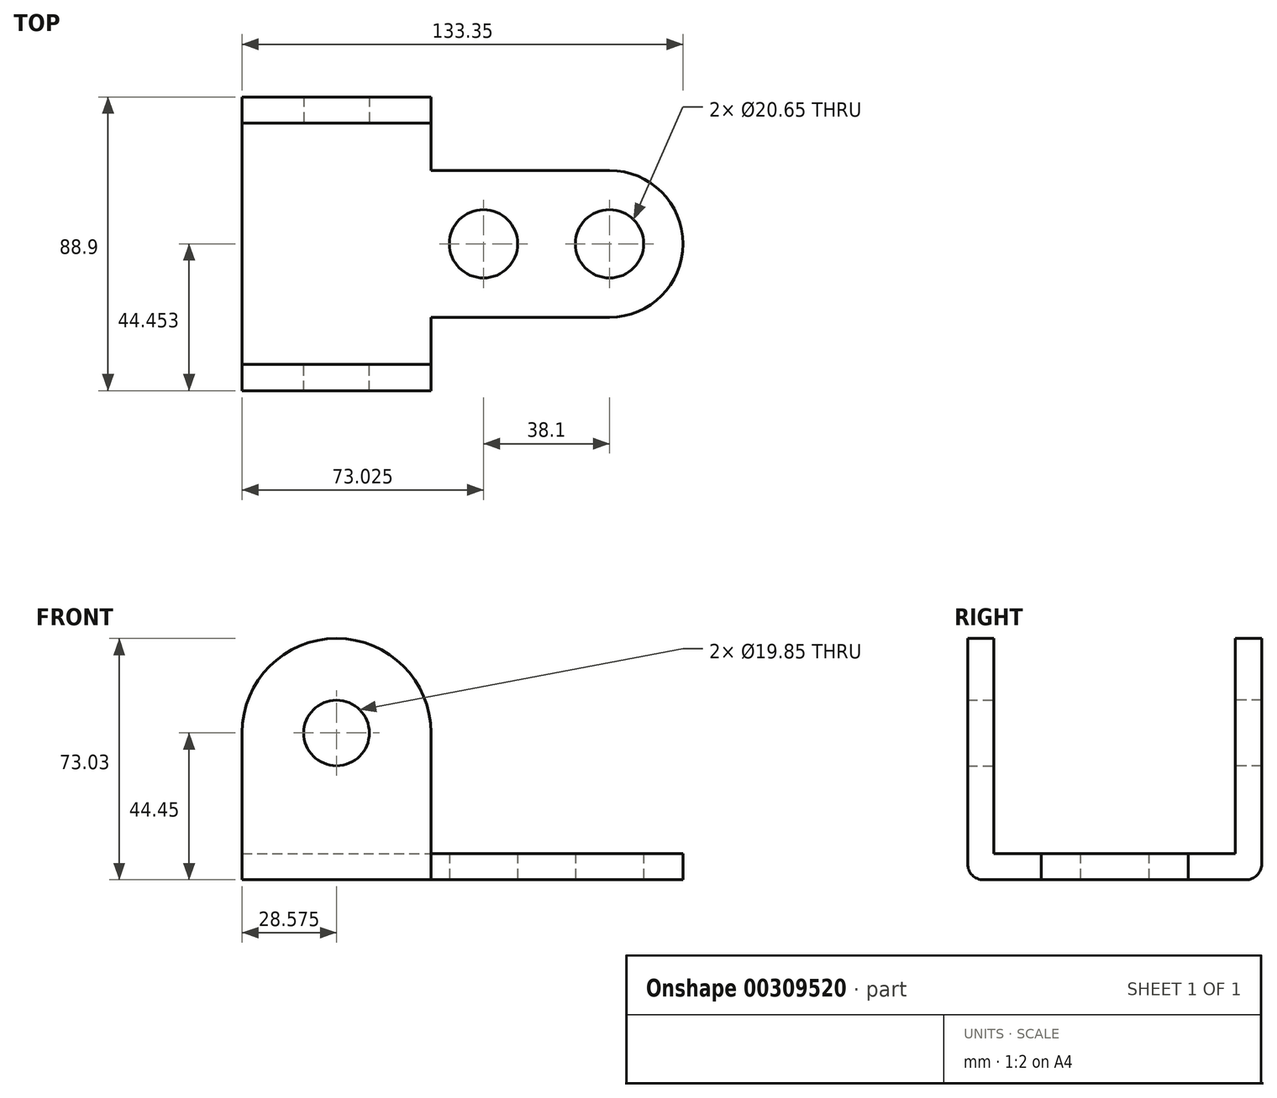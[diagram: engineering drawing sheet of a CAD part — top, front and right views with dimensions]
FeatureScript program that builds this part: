
annotation { "Feature Type Name" : "Feature", "Feature Type Description" : "" }
export const myFeature = defineFeature(function(context is Context, id is Id, definition is map)
    precondition{}
    {
        {
            var Q0;
            Q0=qCreatedBy(makeId("Front.planeOp"),FACE);
            var sketch = newSketch(context, id + "F0", { "sketchPlane" : qUnion([Q0])});
            skLineSegment(sketch, "E0.bottom", {"start": v(0, 0) * mm, "end": v(57.15, 0) * mm});
            skLineSegment(sketch, "E0.left", {"start": v(0, 0) * mm, "end": v(0, 44.45) * mm});
            skLineSegment(sketch, "E0.right", {"start": v(57.15, 0) * mm, "end": v(57.15, 44.45) * mm});
            skCircle(sketch, "E1", {"center": v(28.57, 44.45) * mm, "radius": 9.92 * mm});
            skArc(sketch, "E2", {"start": v(57.15, 44.45) * mm, "mid": v(28.57, 73.03) * mm, "end": v(0, 44.45) * mm});
            skSolve(sketch);
        }
        {
            var Q0;
            Q0 = qSketchRegion(id + "F0", true);
            extrude(context, id + "F1", {"entities" : qUnion([Q0]), "depth" : 7.94 * mm});
        }
        {
            var Q0;
            Q0=qCreatedBy(makeId("Top.planeOp"),FACE);
            var sketch = newSketch(context, id + "F2", { "sketchPlane" : qUnion([Q0])});
            skLineSegment(sketch, "E3.bottom", {"start": v(0, 0) * mm, "end": v(57.15, 0) * mm});
            skLineSegment(sketch, "E3.top", {"start": v(0, 36.51) * mm, "end": v(57.15, 36.51) * mm});
            skLineSegment(sketch, "E3.left", {"start": v(0, 0) * mm, "end": v(0, 36.51) * mm});
            skLineSegment(sketch, "E3.right", {"start": v(57.15, 0) * mm, "end": v(57.15, 36.51) * mm});
            skSolve(sketch);
        }
        {
            var Q0;
            Q0 = qSketchRegion(id + "F2", true);
            extrude(context, id + "F3", {"entities" : qUnion([Q0]), "operationType" : NewBodyOperationType.ADD, "depth" : 7.94 * mm});
        }
        {
            var Q0;
            Q0=makeQuery(id+"F1.opExtrude","SWEPT_BODY",BODY,{"disambiguationData":[OSD([sQuery(id+"F0.wireOp",EDGE,"E0.bottom"),sQuery(id+"F0.wireOp",EDGE,"E0.left"),sQuery(id+"F0.wireOp",EDGE,"E0.right"),sQuery(id+"F0.wireOp",EDGE,"E1"),sQuery(id+"F0.wireOp",EDGE,"E2")])]});
            var Q1;
            Q1=makeQuery(id+"F3.opExtrude","SWEPT_FACE",FACE,{"disambiguationData":[OSD([sQuery(id+"F2.wireOp",EDGE,"E3.top")])]});
            mirror(context, id + "F4", {"operationType" : NewBodyOperationType.ADD, "entities" : qUnion([Q0]), "mirrorPlane" : qUnion([Q1])});
        }
        {
            var Q0;
            Q0=qCreatedBy(makeId("Top.planeOp"),FACE);
            var sketch = newSketch(context, id + "F5", { "sketchPlane" : qUnion([Q0])});
            skLineSegment(sketch, "E4.bottom", {"start": v(57.15, 14.29) * mm, "end": v(111.12, 14.29) * mm});
            skLineSegment(sketch, "E4.top", {"start": v(57.15, 58.74) * mm, "end": v(111.12, 58.74) * mm});
            skLineSegment(sketch, "E4.left", {"start": v(57.15, 14.29) * mm, "end": v(57.15, 58.74) * mm});
            skPoint(sketch, "E5", {"position": v(57.15, 36.51) * mm});
            skArc(sketch, "E6", {"start": v(111.12, 14.29) * mm, "mid": v(133.35, 36.51) * mm, "end": v(111.12, 58.74) * mm});
            skCircle(sketch, "E7", {"center": v(111.12, 36.51) * mm, "radius": 10.33 * mm});
            skCircle(sketch, "E8", {"center": v(73.03, 36.51) * mm, "radius": 10.33 * mm});
            skSolve(sketch);
        }
        {
            var Q0;
            Q0 = qSketchRegion(id + "F5", true);
            extrude(context, id + "F6", {"entities" : qUnion([Q0]), "operationType" : NewBodyOperationType.ADD, "depth" : 7.94 * mm});
        }
        {
            var Q0;
            Q0=makeQuery(id+"F4.opPattern","COPY",EDGE,{"derivedFrom":makeQuery(id+"F3.opExtrude","CAP_EDGE",EDGE,{"disambiguationData":[OSD([sQuery(id+"F2.wireOp",EDGE,"E3.bottom")])],"isStart":false}),"instanceName":"1"});
            var Q1;
            Q1=makeQuery(id+"F3.opExtrude","CAP_EDGE",EDGE,{"disambiguationData":[OSD([sQuery(id+"F2.wireOp",EDGE,"E3.bottom")])],"isStart":false});
            var Q2;
            Q2=makeQuery(id+"F1.opExtrude","CAP_EDGE",EDGE,{"disambiguationData":[OSD([sQuery(id+"F0.wireOp",EDGE,"E0.bottom")])],"isStart":false});
            var Q3;
            Q3=makeQuery(id+"F4.opPattern","COPY",EDGE,{"derivedFrom":makeQuery(id+"F1.opExtrude","CAP_EDGE",EDGE,{"disambiguationData":[OSD([sQuery(id+"F0.wireOp",EDGE,"E0.bottom")])],"isStart":false}),"instanceName":"1"});
            fillet(context, id + "F7", {"entities" : qUnion([Q0, Q1, Q2, Q3]), "radius" : 4.76 * mm, "tangentPropagation" : true, "allowEdgeOverflow" : false});
        }
    });
